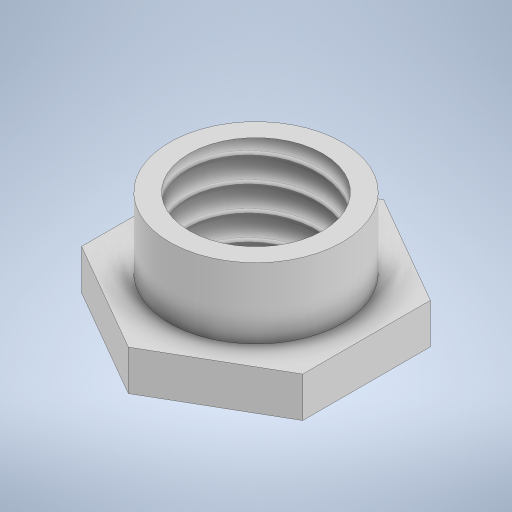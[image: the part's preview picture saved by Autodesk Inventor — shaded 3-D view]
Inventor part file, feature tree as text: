
AUTODESK INVENTOR PART (.ipt)
format: ipt  version: 2023 (Build 270158030, 158C)  size: 262,656 bytes
history: native  units: mm
features: sketch x3, extrude x2, hole x1
ambient origin geometry x8: Origin, YZ Plane, XZ Plane, XY Plane, X Axis, Y Axis, Z Axis, Center Point
bodies: Solid1 (feature_tree)
feature tree (6):
  extrude  "Extrusion1"  Depth=2.0mm TaperAngle=0.0deg
  extrude  "Extrusion2"  Depth=3.5mm TaperAngle=0.0deg
  hole  "Hole1"  [1 undecoded]
  sketch  "Sketch1"  dims[d0=11.0mm d1=2.0mm d2=0.0mm]
  sketch  "Sketch2"  dims[d3=8.6mm d4=3.5mm d5=0.0mm]
  sketch  "Sketch3"  dims[d6=8.0mm d7=6.647mm d8=16.0mm d9=4.0mm d10=2.0mm d11=90.0deg d12=8.0mm d13=0.0mm]
note: 1 required parameter value undecoded (feature->parameter linkage not recoverable at this tier; creation-order binding heuristic only, values carry confidence <= 0.55)
